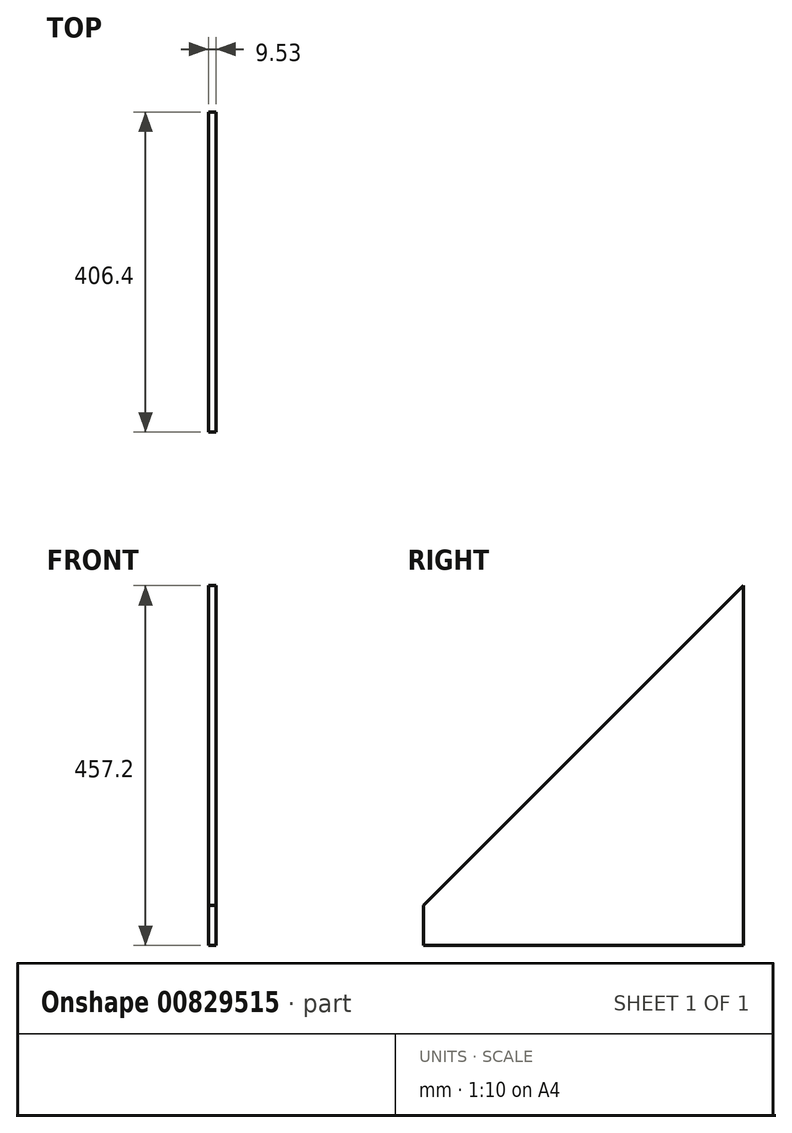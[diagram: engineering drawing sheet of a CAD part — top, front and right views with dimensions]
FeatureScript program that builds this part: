
annotation { "Feature Type Name" : "Feature", "Feature Type Description" : "" }
export const myFeature = defineFeature(function(context is Context, id is Id, definition is map)
    precondition{}
    {
        {
            var Q0;
            Q0=qCreatedBy(makeId("Right.planeOp"),FACE);
            var sketch = newSketch(context, id + "F0", { "sketchPlane" : qUnion([Q0])});
            skLineSegment(sketch, "E0.bottom", {"start": v(-203.2, -25.4) * mm, "end": v(203.2, -25.4) * mm});
            skLineSegment(sketch, "E0.left", {"start": v(-203.2, -25.4) * mm, "end": v(-203.2, 25.4) * mm});
            skPoint(sketch, "E0.middle", {"position": v(0, 0) * mm});
            skLineSegment(sketch, "E1", {"start": v(203.2, 431.8) * mm, "end": v(-203.2, 25.4) * mm});
            skLineSegment(sketch, "E2", {"start": v(203.2, -25.4) * mm, "end": v(203.2, 431.8) * mm});
            skSolve(sketch);
        }
        {
            var Q0;
            Q0 = qSketchRegion(id + "F0", true);
            extrude(context, id + "F1", {"entities" : qUnion([Q0]), "depth" : 9.52 * mm, "offsetDistance" : 25.4 * mm});
        }
    });
